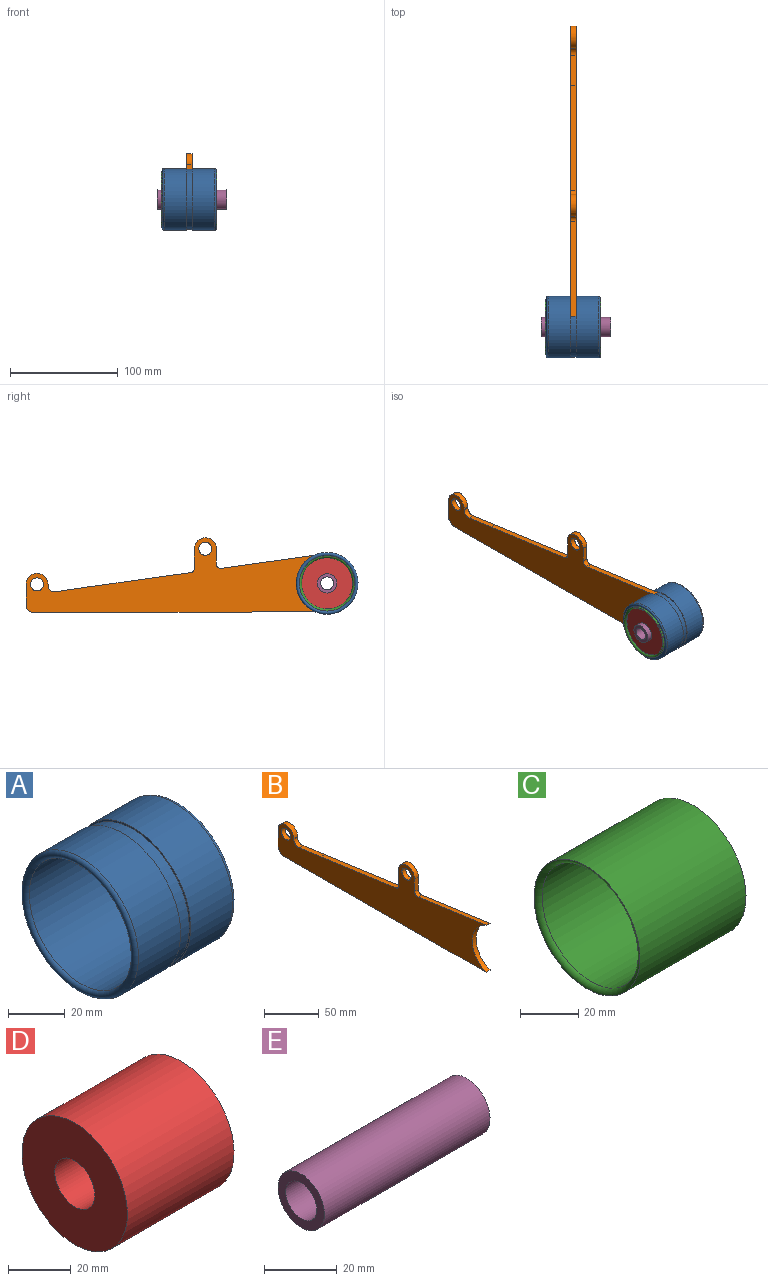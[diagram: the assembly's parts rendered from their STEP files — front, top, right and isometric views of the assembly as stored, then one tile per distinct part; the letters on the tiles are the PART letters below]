
ASSEMBLY  parts=5 mates=4
PART A: 8 faces, bbox 50x62.2x62.2 mm
  f0: cylinder r=28.75mm len=57.5mm, axis (-1,0,0), area 3793.5mm2, adj f5,f6
  f1: cylinder r=25.75mm len=51.5mm, axis (-1,0,0), area 7604.2mm2, adj f6,f7
  f2: cylinder r=28.75mm len=57.5mm, axis (-1,0,0), area 3793.5mm2, adj f4,f7
  f3: cylinder r=28.05mm len=56.1mm, axis (-1,0,0), area 881.2mm2, adj f4,f5
  f4: plane 57.5x57.5mm, normal (-1,0,0), area 124.9mm2, adj f2,f3
  f5: plane 57.5x57.5mm, normal (1,0,0), area 124.9mm2, adj f0,f3
  f6: torus R=27.25mm, axis (1,0,0), area 806.8mm2, adj f0,f1
  f7: torus R=27.25mm, axis (1,0,0), area 806.8mm2, adj f1,f2
PART B: 21 faces, bbox 5x270x69.9 mm
  f0: plane 261.97x5mm, normal (0,0,-1), area 1309.8mm2, adj f1,f17,f19,f20
  f1: cylinder r=8mm len=8.03mm, axis (1,0,0), area 63mm2, adj f0,f2,f19,f20
  f2: plane 18.49x5mm, normal (0,1,0), area 92.4mm2, adj f1,f3,f19,f20
  f3: cylinder r=10.25mm len=20.5mm, axis (1,0,0), area 161mm2, adj f2,f4,f19,f20
  f4: plane 5x0.89mm, normal (0,-1,0), area 4.5mm2, adj f3,f5,f19,f20
  f5: cylinder r=6mm len=6.88mm, axis (1,0,0), area 51.5mm2, adj f4,f6,f19,f20
  f6: plane 28.17x5mm, normal (0,0.15,0.99), area 142.4mm2, adj f5,f7,f19,f20
  f7: plane 97.53x13.66mm, normal (0,0.14,0.99), area 492.4mm2, adj f6,f8,f19,f20
  f8: cylinder r=4mm len=5mm, axis (1,0,0), area 28.6mm2, adj f7,f9,f19,f20
  f9: plane 18.18x5mm, normal (0,1,0), area 90.9mm2, adj f8,f10,f19,f20
  f10: cylinder r=10.25mm len=20.5mm, axis (1,0,0), area 161mm2, adj f9,f11,f19,f20
  f11: plane 14.28x5mm, normal (0,-1,0), area 71.4mm2, adj f10,f12,f19,f20
  f12: cylinder r=4mm len=5mm, axis (1,0,0), area 34.1mm2, adj f11,f13,f19,f20
  f13: plane 88.36x12.37mm, normal (0,0.14,0.99), area 446.1mm2, adj f12,f14,f19,f20
  f14: plane 5x0.17mm, normal (0,-1,0), area 0.9mm2, adj f13,f15,f19,f20
  f15: cylinder r=28.05mm len=52.41mm, axis (1,0,0), area 338.4mm2, adj f14,f17,f19,f20
  f16: cylinder r=6mm len=12mm, axis (1,0,0), area 188.5mm2, adj f19,f20
  f17: plane 5x0.17mm, normal (0,-1,0), area 0.9mm2, adj f0,f15,f19,f20
  f18: cylinder r=6mm len=12mm, axis (1,0,0), area 188.5mm2, adj f19,f20
  f19: plane 270x69.91mm, normal (-1,0,0), area 9310.4mm2, adj f0,f1,f2,f3,f4,f5,f6,f7
  f20: plane 270x69.91mm, normal (1,0,0), area 9310.4mm2, adj f0,f1,f2,f3,f4,f5,f6,f7
PART C: 4 faces, bbox 51.6x58.8x58.8 mm
  f0: cylinder r=23.75mm len=47.6mm, axis (-1,0,0), area 7103.1mm2, adj f2,f3
  f1: cylinder r=25.75mm len=51.6mm, axis (-1,0,0), area 8348.5mm2, adj f2,f3
  f2: torus R=25.75mm, axis (1,0,0), area 483.2mm2, adj f0,f1
  f3: torus R=25.75mm, axis (1,0,0), area 483.2mm2, adj f0,f1
PART D: 4 faces, bbox 48x47.5x47.5 mm
  f0: cylinder r=9mm len=48mm, axis (-1,0,0), area 2714.3mm2, adj f2,f3
  f1: cylinder r=23.75mm len=48mm, axis (-1,0,0), area 7162.8mm2, adj f2,f3
  f2: plane 47.5x47.5mm, normal (1,0,0), area 1517.6mm2, adj f0,f1
  f3: plane 47.5x47.5mm, normal (-1,0,0), area 1517.6mm2, adj f0,f1
PART E: 4 faces, bbox 64.2x18x18 mm
  f0: cylinder r=6mm len=64.2mm, axis (-1,0,0), area 2420.3mm2, adj f2,f3
  f1: cylinder r=9mm len=64.2mm, axis (-1,0,0), area 3630.4mm2, adj f2,f3
  f2: plane 18x18mm, normal (1,0,0), area 141.4mm2, adj f0,f1
  f3: plane 18x18mm, normal (-1,0,0), area 141.4mm2, adj f0,f1
PLACE A t=(-78.32,-81.56,141.93)mm
PLACE B t=(-50.82,198.44,114.43)mm
PLACE C t=(-53.62,-81.56,141.93)mm
PLACE D t=(-53.62,-81.56,141.93)mm
PLACE E t=(-50.82,-81.56,141.93)mm
MATE fastened C.f0 <-> D.f0  axis (-1,0,0) through (-53.62,-81.56,141.93)mm
MATE fastened A.f1 <-> C.f1  axis (1,0,0) through (-29.82,-81.56,141.93)mm
MATE fastened A.f0 <-> E.f1  axis (-1,0,0) through (-50.82,-81.56,141.93)mm
MATE fastened B.f15 <-> A.f3  axis (1,0,0) through (-50.82,-81.56,141.93)mm
